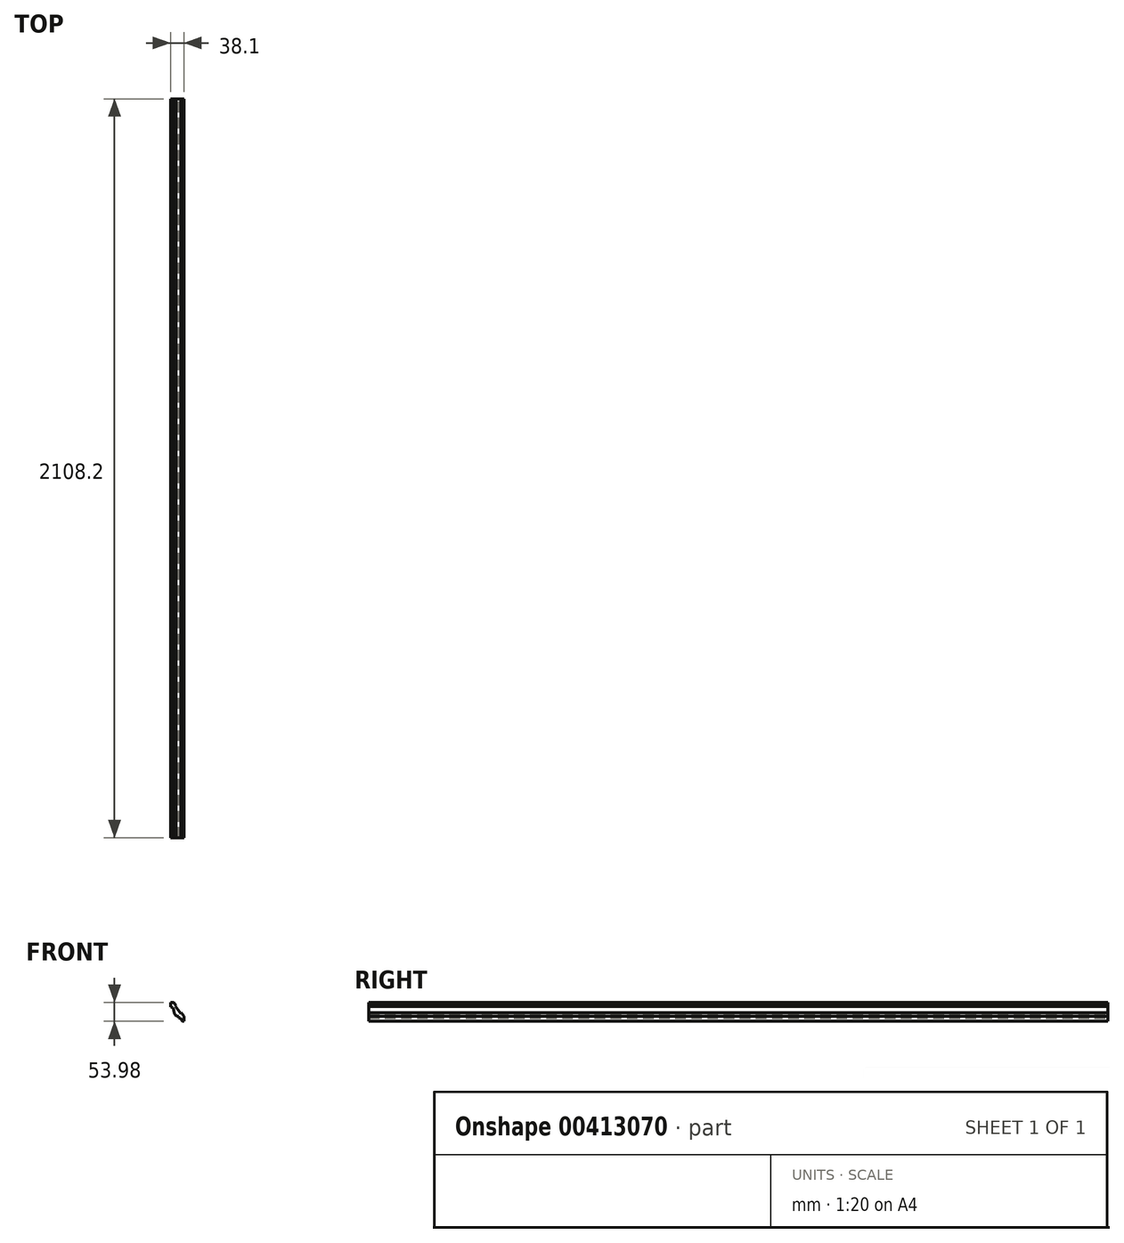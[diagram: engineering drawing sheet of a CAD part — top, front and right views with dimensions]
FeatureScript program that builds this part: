
annotation { "Feature Type Name" : "Feature", "Feature Type Description" : "" }
export const myFeature = defineFeature(function(context is Context, id is Id, definition is map)
    precondition{}
    {
        {
            var Q0;
            Q0=qCreatedBy(makeId("Front.planeOp"),FACE);
            var sketch = newSketch(context, id + "F0", { "sketchPlane" : qUnion([Q0])});
            skLineSegment(sketch, "E0", {"start": v(-5.33, 0) * mm, "end": v(0, 0) * mm});
            skLineSegment(sketch, "E1", {"start": v(0, 0) * mm, "end": v(0, 14.48) * mm});
            skLineSegment(sketch, "E2", {"start": v(-29.2, 53.98) * mm, "end": v(-38.1, 53.98) * mm});
            skLineSegment(sketch, "E3", {"start": v(-38.1, 53.98) * mm, "end": v(-38.1, 41.66) * mm});
            skLineSegment(sketch, "E4", {"start": v(0, 14.48) * mm, "end": v(-7.05, 24.02) * mm});
            skLineSegment(sketch, "E5", {"start": v(-7.05, 24.02) * mm, "end": v(-9.1, 22.5) * mm});
            skLineSegment(sketch, "E6", {"start": v(-9.1, 22.5) * mm, "end": v(-24.2, 42.93) * mm});
            skLineSegment(sketch, "E7", {"start": v(-24.2, 42.93) * mm, "end": v(-22.16, 44.44) * mm});
            skLineSegment(sketch, "E8", {"start": v(-22.16, 44.44) * mm, "end": v(-29.2, 53.98) * mm});
            skLineSegment(sketch, "E9", {"start": v(-14.86, 9.53) * mm, "end": v(-14.86, 14.6) * mm});
            skArc(sketch, "E10", {"start": v(-5.33, 0) * mm, "mid": v(-8.12, 6.74) * mm, "end": v(-14.86, 9.53) * mm});
            skFitSpline(sketch, "E11", {"points": [v(-38.1, 41.66) * mm, v(-27.86, 25.6) * mm, v(-14.86, 14.6) * mm], "startDerivative": vector(58.03, -11.78) * mm, "endDerivative": vector(50.48, 1.67) * mm});
            skPoint(sketch, "E12.orphan", {"position": v(-38.1, 0) * mm});
            skSolve(sketch);
        }
        {
            var Q0;
            Q0=qSketchRegion(id+"F0",true);
            extrude(context, id + "F1", {"entities" : qUnion([Q0]), "depth" : 2108.2 * mm});
        }
    });
